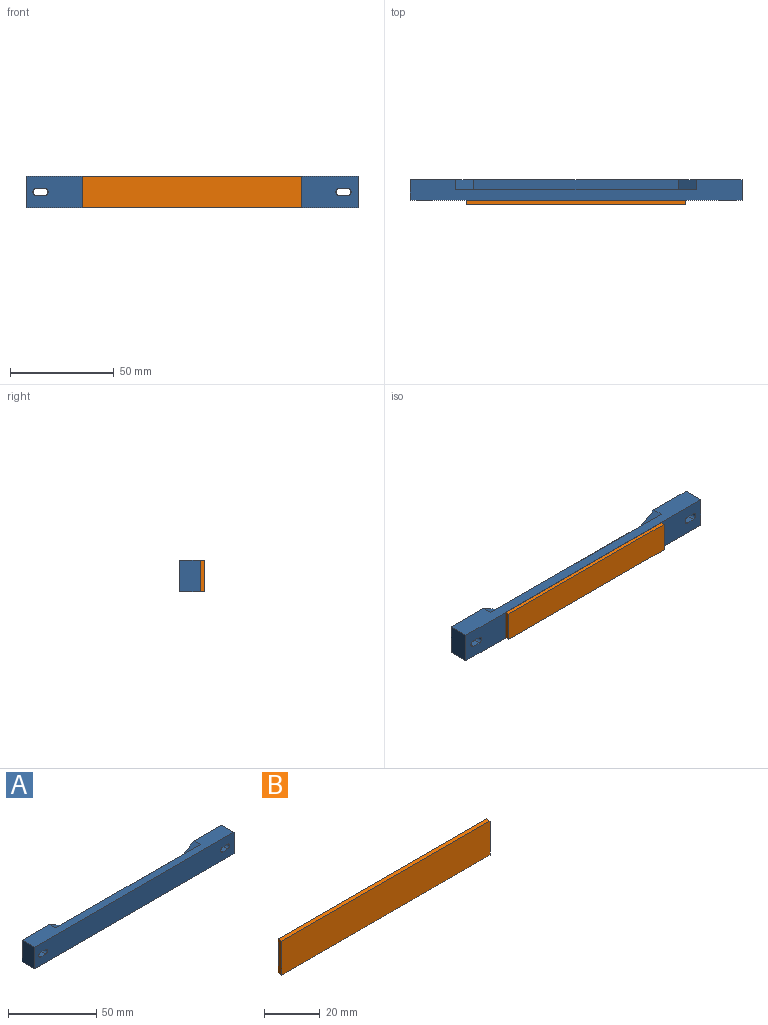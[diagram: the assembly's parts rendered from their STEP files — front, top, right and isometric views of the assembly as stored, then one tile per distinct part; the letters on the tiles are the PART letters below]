
ASSEMBLY  parts=2 mates=1
PART A: 32 faces, bbox 160x10x15 mm
  f0: plane 160x15mm, normal (0,-1,0), area 2356.5mm2, adj f4,f5,f6,f7,f24,f25,f26,f27
  f1: plane 11x7mm, normal (0,1,0), area 44.7mm2, adj f16,f17,f18,f19,f28,f29,f30,f31
  f2: plane 11x7mm, normal (0,1,0), area 44.7mm2, adj f20,f21,f22,f23,f24,f25,f26,f27
  f3: plane 160x15mm, normal (0,1,0), area 1193.6mm2, adj f4,f5,f6,f7,f8,f9,f10,f12
  f4: plane 160x10mm, normal (0,0,1), area 1020mm2, adj f0,f3,f6,f7,f8,f10,f11
  f5: plane 160x10mm, normal (0,0,-1), area 1020mm2, adj f0,f3,f6,f7,f12,f13,f15
  f6: plane 15x10mm, normal (1,0,0), area 150mm2, adj f0,f3,f4,f5
  f7: plane 15x10mm, normal (-1,0,0), area 150mm2, adj f0,f3,f4,f5
  f8: plane 8.66x5mm, normal (-0.5,0,0.87), area 50mm2, adj f3,f4,f9,f11
  f9: plane 98.68x5mm, normal (0,0,1), area 493.4mm2, adj f3,f8,f10,f11
  f10: plane 8.66x5mm, normal (0.5,0,0.87), area 50mm2, adj f3,f4,f9,f11
  f11: plane 116x5mm, normal (0,1,0), area 536.7mm2, adj f4,f8,f9,f10
  f12: plane 8.66x5mm, normal (-0.5,0,-0.87), area 50mm2, adj f3,f5,f14,f15
  f13: plane 8.66x5mm, normal (0.5,0,-0.87), area 50mm2, adj f3,f5,f14,f15
  f14: plane 98.68x5mm, normal (0,0,-1), area 493.4mm2, adj f3,f12,f13,f15
  f15: plane 116x5mm, normal (0,1,0), area 536.7mm2, adj f5,f12,f13,f14
  f16: cylinder r=3.5mm len=7mm, axis (0,1,0), area 33mm2, adj f1,f3,f17,f19
  f17: plane 4x3mm, normal (0,0,1), area 12mm2, adj f1,f3,f16,f18
  f18: cylinder r=3.5mm len=7mm, axis (0,1,0), area 33mm2, adj f1,f3,f17,f19
  f19: plane 4x3mm, normal (0,0,-1), area 12mm2, adj f1,f3,f16,f18
  f20: cylinder r=3.5mm len=7mm, axis (0,1,0), area 33mm2, adj f2,f3,f21,f23
  f21: plane 4x3mm, normal (0,0,-1), area 12mm2, adj f2,f3,f20,f22
  f22: cylinder r=3.5mm len=7mm, axis (0,1,0), area 33mm2, adj f2,f3,f21,f23
  f23: plane 4x3mm, normal (0,0,1), area 12mm2, adj f2,f3,f20,f22
  f24: cylinder r=1.65mm len=7mm, axis (0,1,0), area 36.3mm2, adj f0,f2,f25,f27
  f25: plane 7x4mm, normal (0,0,-1), area 28mm2, adj f0,f2,f24,f26
  f26: cylinder r=1.65mm len=7mm, axis (0,1,0), area 36.3mm2, adj f0,f2,f25,f27
  f27: plane 7x4mm, normal (0,0,1), area 28mm2, adj f0,f2,f24,f26
  f28: cylinder r=1.65mm len=7mm, axis (0,1,0), area 36.3mm2, adj f0,f1,f29,f31
  f29: plane 7x4mm, normal (0,0,1), area 28mm2, adj f0,f1,f28,f30
  f30: cylinder r=1.65mm len=7mm, axis (0,1,0), area 36.3mm2, adj f0,f1,f29,f31
  f31: plane 7x4mm, normal (0,0,-1), area 28mm2, adj f0,f1,f28,f30
PART B: 6 faces, bbox 106x2x15 mm
  f0: plane 106x2mm, normal (0,0,-1), area 212mm2, adj f1,f3,f4,f5
  f1: plane 15x2mm, normal (1,0,0), area 30mm2, adj f0,f2,f4,f5
  f2: plane 106x2mm, normal (0,0,1), area 212mm2, adj f1,f3,f4,f5
  f3: plane 15x2mm, normal (-1,0,0), area 30mm2, adj f0,f2,f4,f5
  f4: plane 106x15mm, normal (0,-1,0), area 1590mm2, adj f0,f1,f2,f3
  f5: plane 106x15mm, normal (0,1,0), area 1590mm2, adj f0,f1,f2,f3
PLACE A t=(-7.63,-4.41,7.48)mm
PLACE B t=(-7.63,-4.41,7.48)mm
MATE fastened B.f5 <-> A.f0  axis (0,1,0) through (-7.63,-4.41,7.48)mm
